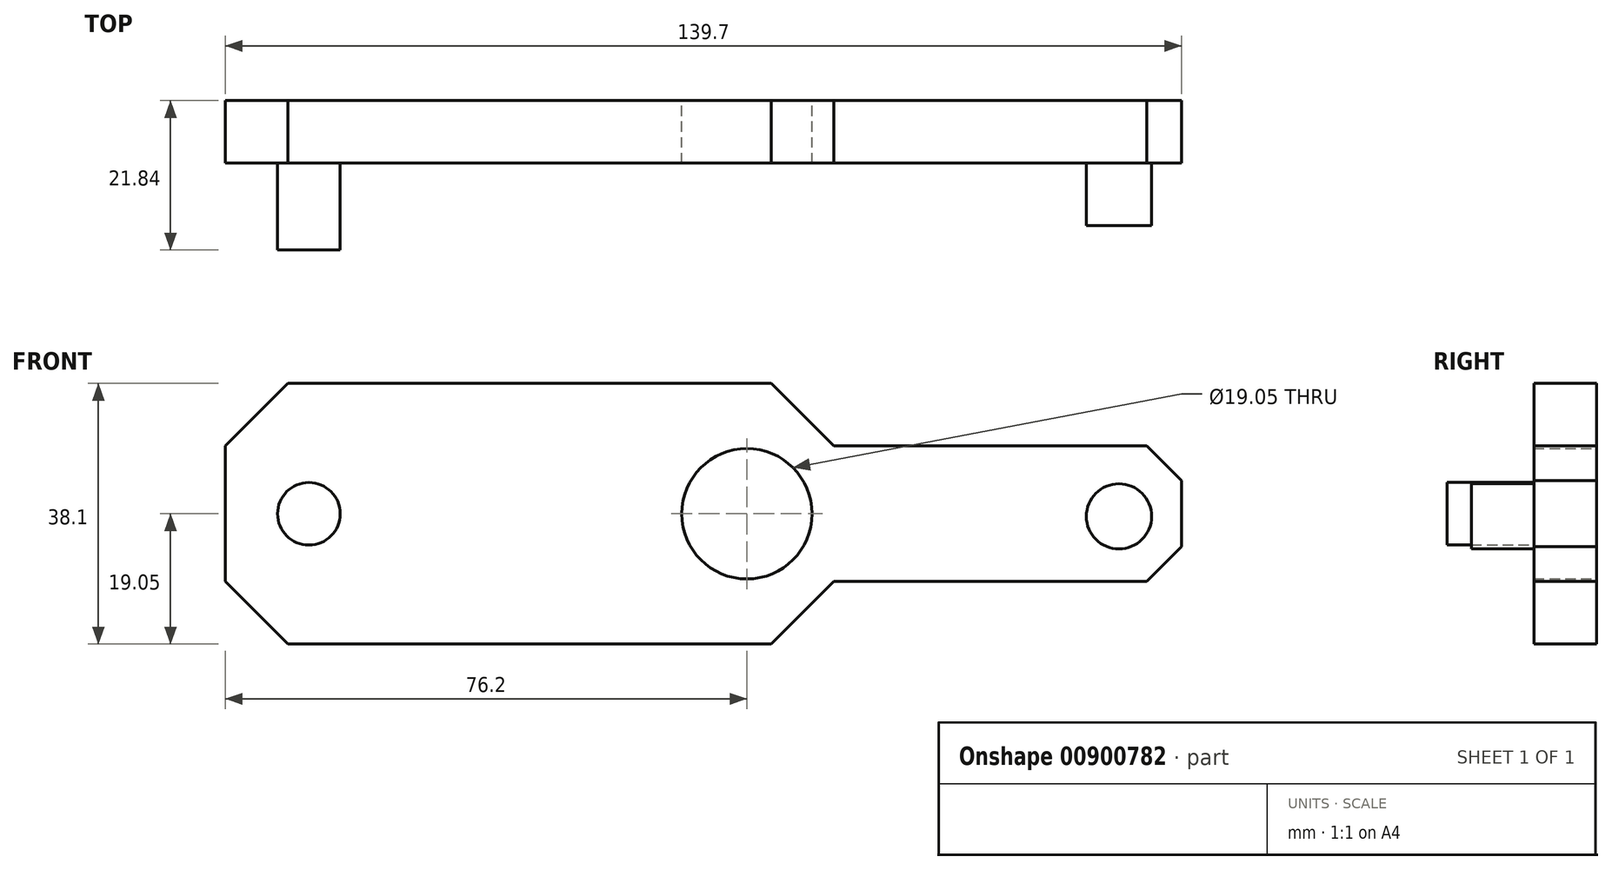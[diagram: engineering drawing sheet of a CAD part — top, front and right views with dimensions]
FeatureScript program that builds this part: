
annotation { "Feature Type Name" : "Feature", "Feature Type Description" : "" }
export const myFeature = defineFeature(function(context is Context, id is Id, definition is map)
    precondition{}
    {
        {
            var Q0;
            Q0=qCreatedBy(makeId("Front.planeOp"),FACE);
            var sketch = newSketch(context, id + "F0", { "sketchPlane" : qUnion([Q0])});
            skLineSegment(sketch, "E0.bottom", {"start": v(0, 0) * mm, "end": v(88.9, 0) * mm});
            skLineSegment(sketch, "E0.top", {"start": v(0, 38.1) * mm, "end": v(88.9, 38.1) * mm});
            skLineSegment(sketch, "E0.left", {"start": v(0, 0) * mm, "end": v(0, 38.1) * mm});
            skLineSegment(sketch, "E0.right", {"start": v(88.9, 0) * mm, "end": v(88.9, 38.1) * mm});
            skSolve(sketch);
        }
        {
            var Q0;
            Q0=makeQuery(id+"F0.imprint","IMPRINT",FACE,{"disambiguationData":[TD([[makeQuery(id+"F0.imprint","IMPRINT",EDGE,{"derivedFrom":sQuery(id+"F0.wireOp",EDGE,"E0.bottom")}),1.0]])]});
            extrude(context, id + "F1", {"entities" : qUnion([Q0]), "depth" : 9.14 * mm, "offsetDistance" : 25.4 * mm});
        }
        {
            var Q0;
            Q0=makeQuery(id+"F1.opExtrude","CAP_FACE",FACE,{"disambiguationData":[OSD([sQuery(id+"F0.wireOp",EDGE,"E0.bottom"),sQuery(id+"F0.wireOp",EDGE,"E0.top"),sQuery(id+"F0.wireOp",EDGE,"E0.left"),sQuery(id+"F0.wireOp",EDGE,"E0.right")])],"isStart":false});
            var sketch = newSketch(context, id + "F2", { "sketchPlane" : qUnion([Q0])});
            skCircle(sketch, "E1", {"center": v(12.2, 19.05) * mm, "radius": 4.57 * mm});
            skSolve(sketch);
        }
        {
            var Q0;
            Q0=makeQuery(id+"F2.imprint","IMPRINT",FACE,{"disambiguationData":[TD([[makeQuery(id+"F2.imprint","IMPRINT",EDGE,{"derivedFrom":sQuery(id+"F2.wireOp",EDGE,"E1")}),1.0]])]});
            extrude(context, id + "F3", {"entities" : qUnion([Q0]), "operationType" : NewBodyOperationType.ADD, "depth" : 12.7 * mm, "offsetDistance" : 25.4 * mm});
        }
        {
            var Q0;
            Q0=makeQuery(id+"F1.opExtrude","CAP_FACE",FACE,{"disambiguationData":[OSD([sQuery(id+"F0.wireOp",EDGE,"E0.bottom"),sQuery(id+"F0.wireOp",EDGE,"E0.top"),sQuery(id+"F0.wireOp",EDGE,"E0.left"),sQuery(id+"F0.wireOp",EDGE,"E0.right")])],"isStart":true});
            var sketch = newSketch(context, id + "F4", { "sketchPlane" : qUnion([Q0])});
            skCircle(sketch, "E2", {"center": v(-76.2, 19.05) * mm, "radius": 9.52 * mm});
            skSolve(sketch);
        }
        {
            var Q0;
            Q0=makeQuery(id+"F4.imprint","IMPRINT",FACE,{"disambiguationData":[TD([[makeQuery(id+"F4.imprint","IMPRINT",EDGE,{"derivedFrom":sQuery(id+"F4.wireOp",EDGE,"E2")}),1.0]])]});
            extrude(context, id + "F5", {"entities" : qUnion([Q0]), "operationType" : NewBodyOperationType.REMOVE, "endBound" : BoundingType.THROUGH_ALL, "oppositeDirection" : true, "depth" : 25.4 * mm, "offsetDistance" : 25.4 * mm});
        }
        {
            var Q0;
            Q0=makeQuery(id+"F1.opExtrude","SWEPT_EDGE",EDGE,{"disambiguationData":[OSD([sQuery(id+"F0.wireOp",EDGE,"E0.top"),sQuery(id+"F0.wireOp",EDGE,"E0.left")])]});
            var Q1;
            Q1=makeQuery(id+"F1.opExtrude","SWEPT_EDGE",EDGE,{"disambiguationData":[OSD([sQuery(id+"F0.wireOp",EDGE,"E0.top"),sQuery(id+"F0.wireOp",EDGE,"E0.right")])]});
            var Q2;
            Q2=makeQuery(id+"F1.opExtrude","SWEPT_EDGE",EDGE,{"disambiguationData":[OSD([sQuery(id+"F0.wireOp",EDGE,"E0.bottom"),sQuery(id+"F0.wireOp",EDGE,"E0.left")])]});
            var Q3;
            Q3=makeQuery(id+"F1.opExtrude","SWEPT_EDGE",EDGE,{"disambiguationData":[OSD([sQuery(id+"F0.wireOp",EDGE,"E0.bottom"),sQuery(id+"F0.wireOp",EDGE,"E0.right")])]});
            chamfer(context, id + "F6", {"entities" : qUnion([Q0, Q1, Q2, Q3]), "width" : 9.14 * mm, "tangentPropagation" : true});
        }
        {
            var Q0;
            Q0=makeQuery(id+"F1.opExtrude","SWEPT_FACE",FACE,{"disambiguationData":[OSD([sQuery(id+"F0.wireOp",EDGE,"E0.right")])]});
            var sketch = newSketch(context, id + "F7", { "sketchPlane" : qUnion([Q0])});
            skSolve(sketch);
        }
        {
            var Q0;
            {var subQ0=sQuery(id+"F0.wireOp",EDGE,"E0.right");Q0=makeQuery(id+"F7.imprint","IMPRINT",FACE,{"disambiguationData":[TD([[makeQuery(id+"F7.imprint","IMPRINT",EDGE,{"derivedFrom":makeQuery(id+"F1.opExtrude","CAP_EDGE",EDGE,{"disambiguationData":[OSD([subQ0])],"isStart":true})}),1.0]])]});}
            extrude(context, id + "F8", {"entities" : qUnion([Q0]), "operationType" : NewBodyOperationType.ADD, "depth" : 50.8 * mm, "offsetDistance" : 25.4 * mm});
        }
        {
            var Q0;
            Q0=makeQuery(id+"F8.opExtrude","CAP_EDGE",EDGE,{"disambiguationData":[OSD([sQuery(id+"F0.wireOp",EDGE,"E0.top"),sQuery(id+"F0.wireOp",EDGE,"E0.right")])],"isStart":false});
            var Q1;
            Q1=makeQuery(id+"F8.opExtrude","CAP_EDGE",EDGE,{"disambiguationData":[OSD([sQuery(id+"F0.wireOp",EDGE,"E0.bottom"),sQuery(id+"F0.wireOp",EDGE,"E0.right")])],"isStart":false});
            chamfer(context, id + "F9", {"entities" : qUnion([Q0, Q1]), "width" : 5.08 * mm, "tangentPropagation" : true});
        }
        {
            var Q0;
            {var subQ0=sQuery(id+"F0.wireOp",EDGE,"E0.right");Q0=makeQuery(id+"F8.boolean.opBoolean","MERGE",FACE,{"derivedFrom":[makeQuery(id+"F1.opExtrude","CAP_FACE",FACE,{"disambiguationData":[OSD([sQuery(id+"F0.wireOp",EDGE,"E0.bottom"),sQuery(id+"F0.wireOp",EDGE,"E0.top"),sQuery(id+"F0.wireOp",EDGE,"E0.left"),subQ0])],"isStart":false}),makeQuery(id+"F8.opExtrude","SWEPT_FACE",FACE,{"disambiguationData":[OSD([subQ0]),TDD([makeQuery(id+"F7.imprint","IMPRINT",EDGE,{"derivedFrom":makeQuery(id+"F1.opExtrude","CAP_EDGE",EDGE,{"disambiguationData":[OSD([subQ0])],"isStart":false})})])]})]});}
            var sketch = newSketch(context, id + "F10", { "sketchPlane" : qUnion([Q0])});
            skCircle(sketch, "E3", {"center": v(130.56, 18.67) * mm, "radius": 4.76 * mm});
            skSolve(sketch);
        }
        {
            var Q0;
            Q0=makeQuery(id+"F10.imprint","IMPRINT",FACE,{"disambiguationData":[TD([[makeQuery(id+"F10.imprint","IMPRINT",EDGE,{"derivedFrom":sQuery(id+"F10.wireOp",EDGE,"E3")}),1.0]])]});
            extrude(context, id + "F11", {"entities" : qUnion([Q0]), "operationType" : NewBodyOperationType.ADD, "depth" : 9.14 * mm, "offsetDistance" : 25.4 * mm});
        }
    });
